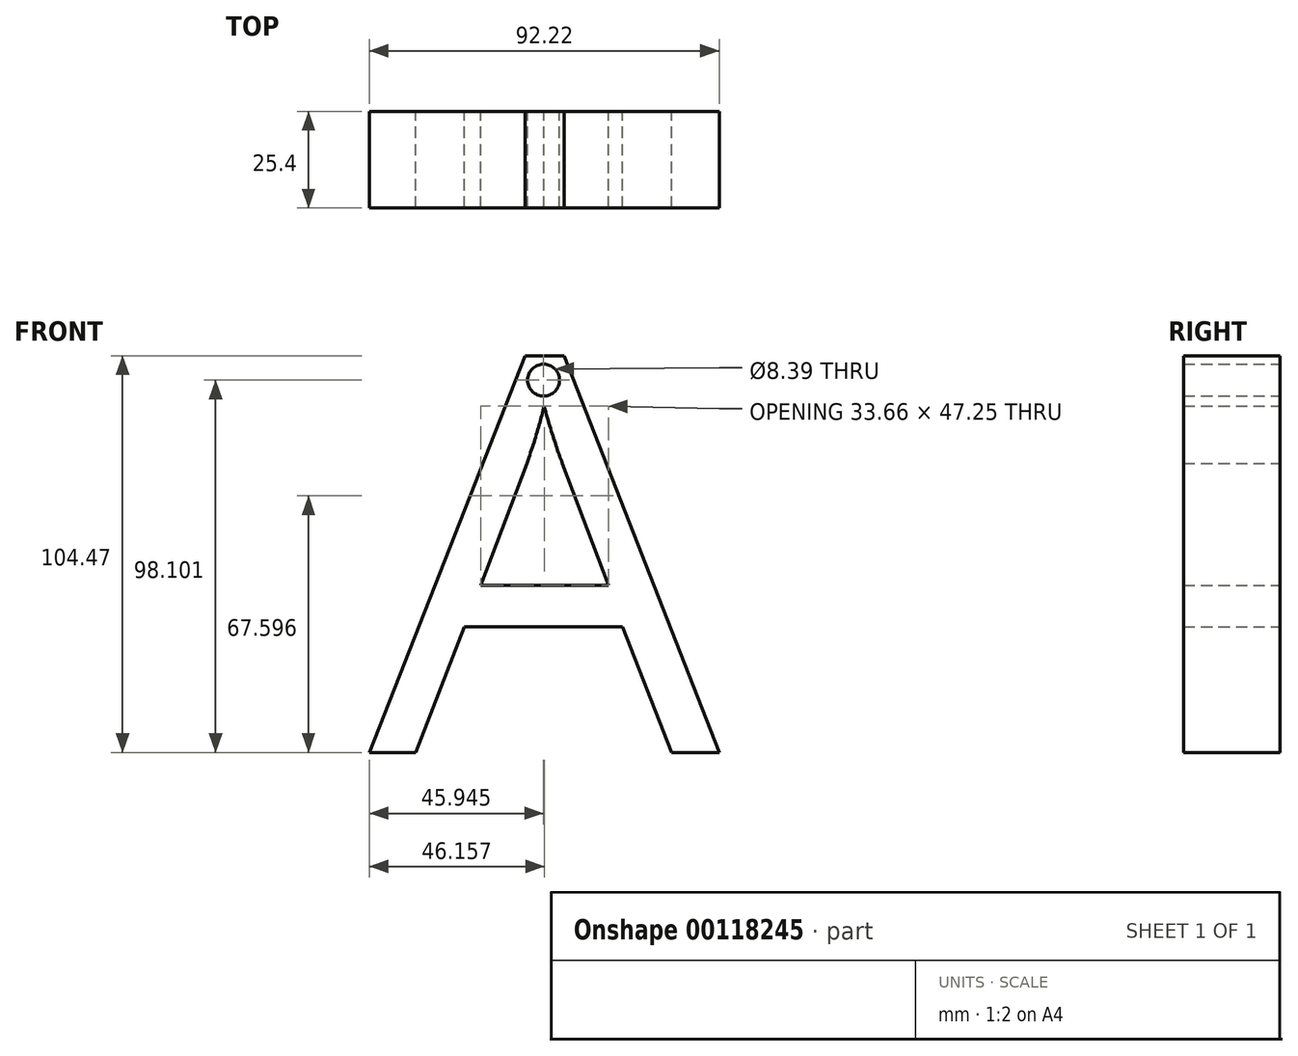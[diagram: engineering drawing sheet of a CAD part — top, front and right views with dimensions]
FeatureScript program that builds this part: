
annotation { "Feature Type Name" : "Feature", "Feature Type Description" : "" }
export const myFeature = defineFeature(function(context is Context, id is Id, definition is map)
    precondition{}
    {
        {
            var Q0;
            Q0=qCreatedBy(makeId("Front.planeOp"),FACE);
            var sketch = newSketch(context, id + "F0", { "sketchPlane" : qUnion([Q0])});
            skText(sketch, "E0", { "text": "A", "fontName": "OpenSans-Regular.ttf"});
            const initialGuessF0  = {"E0": [-0.05993, -0.04833, 1, 0, 0.10493]};
            skSetInitialGuess(sketch, initialGuessF0);
            skSolve(sketch);
        }
        {
            var Q0;
            Q0 = qSketchRegion(id + "F0", true);
            extrude(context, id + "F1", {"entities" : qUnion([Q0]), "depth" : 25.4 * mm});
        }
        {
            var Q0;
            Q0=qCreatedBy(makeId("Front.planeOp"),FACE);
            var sketch = newSketch(context, id + "F2", { "sketchPlane" : qUnion([Q0])});
            skCircle(sketch, "E1", {"center": v(-13.99, 49.77) * mm, "radius": 4.2 * mm});
            skSolve(sketch);
        }
        {
            var Q0;
            Q0 = qSketchRegion(id + "F2", true);
            extrude(context, id + "F3", {"entities" : qUnion([Q0]), "operationType" : NewBodyOperationType.REMOVE, "depth" : 25.4 * mm});
        }
    });
